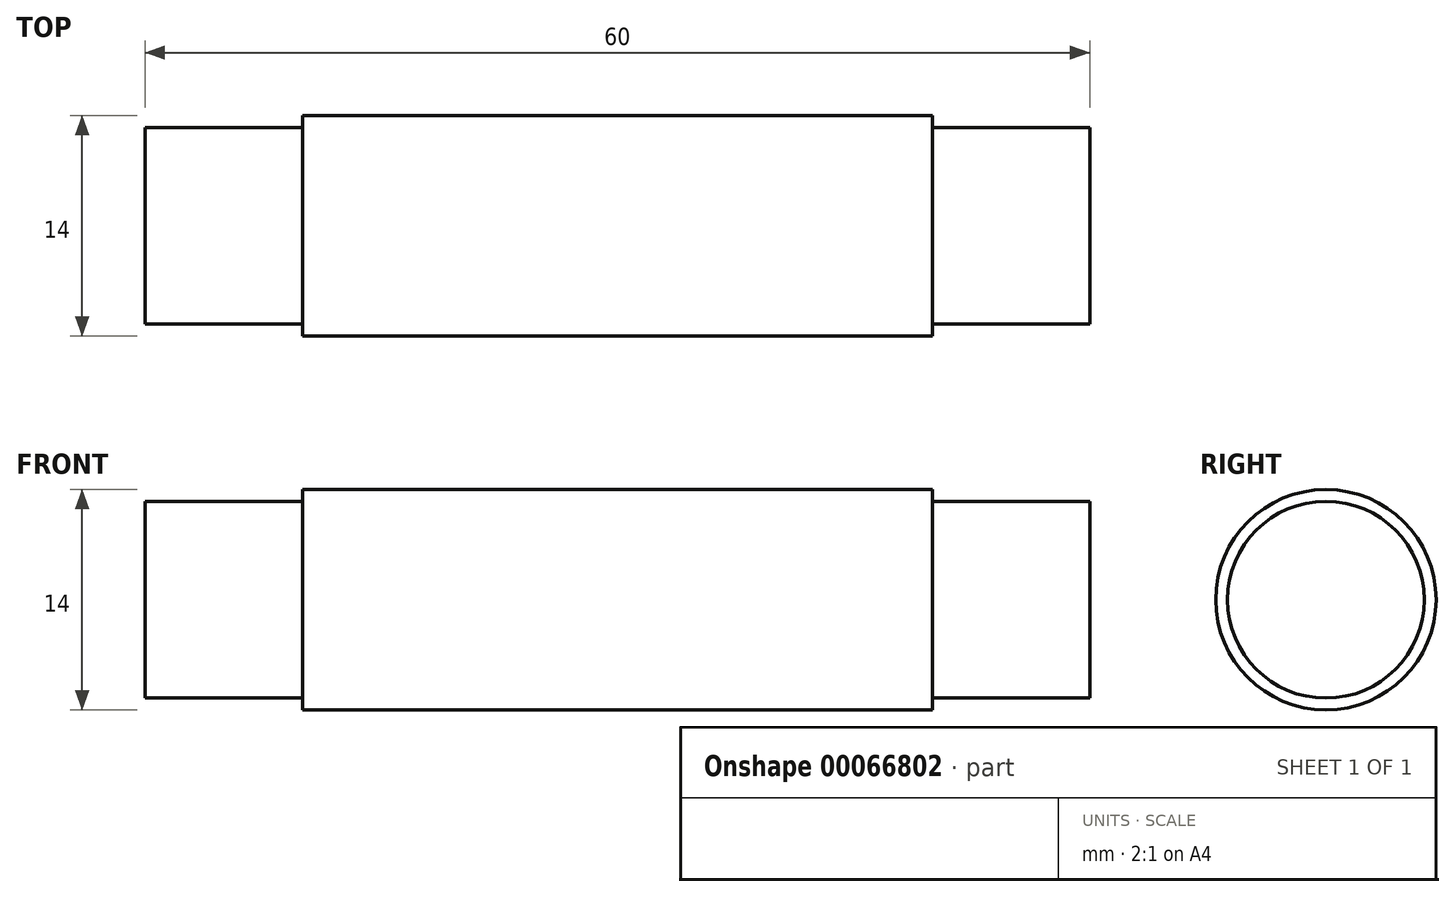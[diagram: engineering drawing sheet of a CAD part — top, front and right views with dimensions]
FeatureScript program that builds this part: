
annotation { "Feature Type Name" : "Feature", "Feature Type Description" : "" }
export const myFeature = defineFeature(function(context is Context, id is Id, definition is map)
    precondition{}
    {
        {
            var Q0;
            Q0=qCreatedBy(makeId("Right.planeOp"),FACE);
            var sketch = newSketch(context, id + "F0", { "sketchPlane" : qUnion([Q0])});
            skCircle(sketch, "E0", {"center": v(0, 0) * mm, "radius": 7 * mm});
            skCircle(sketch, "E1", {"center": v(0, 0) * mm, "radius": 6.25 * mm});
            skSolve(sketch);
        }
        {
            var Q0;
            Q0=makeQuery(id+"F0.imprint","IMPRINT",FACE,{"disambiguationData":[TD([[makeQuery(id+"F0.imprint","IMPRINT",EDGE,{"derivedFrom":sQuery(id+"F0.wireOp",EDGE,"E1")}),1.0]])]});
            extrude(context, id + "F1", {"entities" : qUnion([Q0]), "depth" : 50 * mm, "hasSecondDirection" : true, "secondDirectionOppositeDirection" : true, "secondDirectionDepth" : 10 * mm});
        }
        {
            var Q0;
            Q0=makeQuery(id+"F0.imprint","IMPRINT",FACE,{"disambiguationData":[TD([[makeQuery(id+"F0.imprint","IMPRINT",EDGE,{"derivedFrom":sQuery(id+"F0.wireOp",EDGE,"E0")}),1.0]])]});
            extrude(context, id + "F2", {"entities" : qUnion([Q0]), "operationType" : NewBodyOperationType.ADD, "depth" : 40 * mm});
        }
    });
